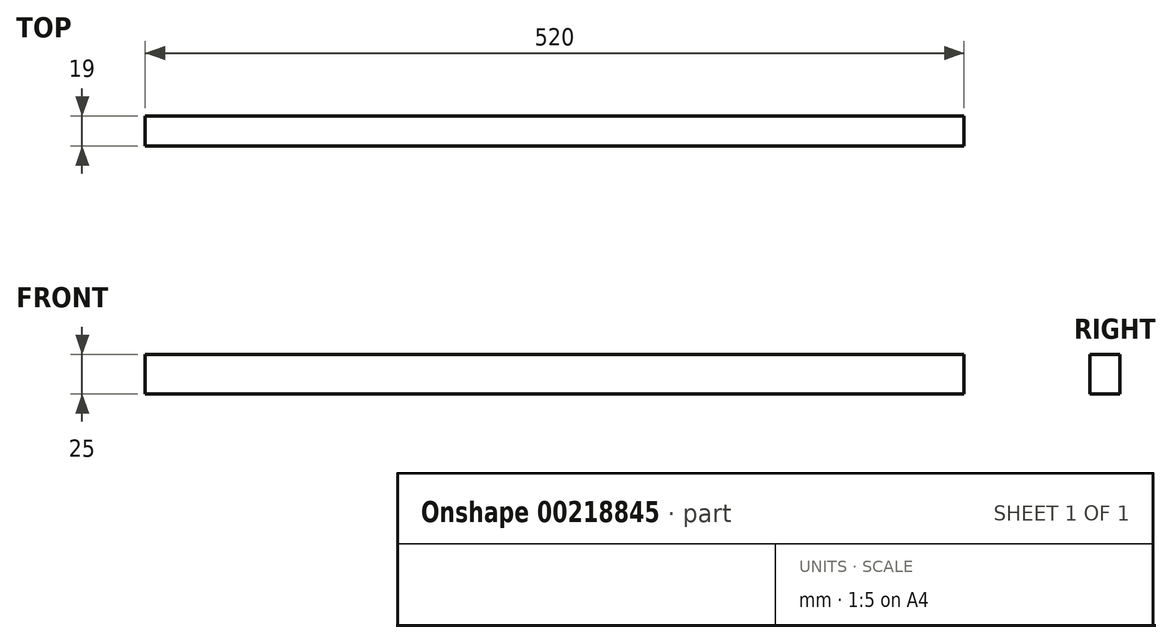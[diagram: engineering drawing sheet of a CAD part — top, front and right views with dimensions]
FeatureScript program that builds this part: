
annotation { "Feature Type Name" : "Feature", "Feature Type Description" : "" }
export const myFeature = defineFeature(function(context is Context, id is Id, definition is map)
    precondition{}
    {
        {
            var Q0;
            Q0=qCreatedBy(makeId("Front.planeOp"),FACE);
            var sketch = newSketch(context, id + "F0", { "sketchPlane" : qUnion([Q0])});
            skLineSegment(sketch, "E0.bottom", {"start": v(260, 12.5) * mm, "end": v(-260, 12.5) * mm});
            skLineSegment(sketch, "E0.top", {"start": v(260, -12.5) * mm, "end": v(-260, -12.5) * mm});
            skLineSegment(sketch, "E0.left", {"start": v(260, 12.5) * mm, "end": v(260, -12.5) * mm});
            skLineSegment(sketch, "E0.right", {"start": v(-260, 12.5) * mm, "end": v(-260, -12.5) * mm});
            skPoint(sketch, "E0.middle", {"position": v(0, 0) * mm});
            skSolve(sketch);
        }
        {
            var Q0;
            Q0=makeQuery(id+"F0.imprint","IMPRINT",FACE,{"disambiguationData":[TD([[makeQuery(id+"F0.imprint","IMPRINT",EDGE,{"derivedFrom":sQuery(id+"F0.wireOp",EDGE,"E0.bottom")}),1.0]])]});
            extrude(context, id + "F1", {"entities" : qUnion([Q0]), "depth" : 19 * mm});
        }
    });
